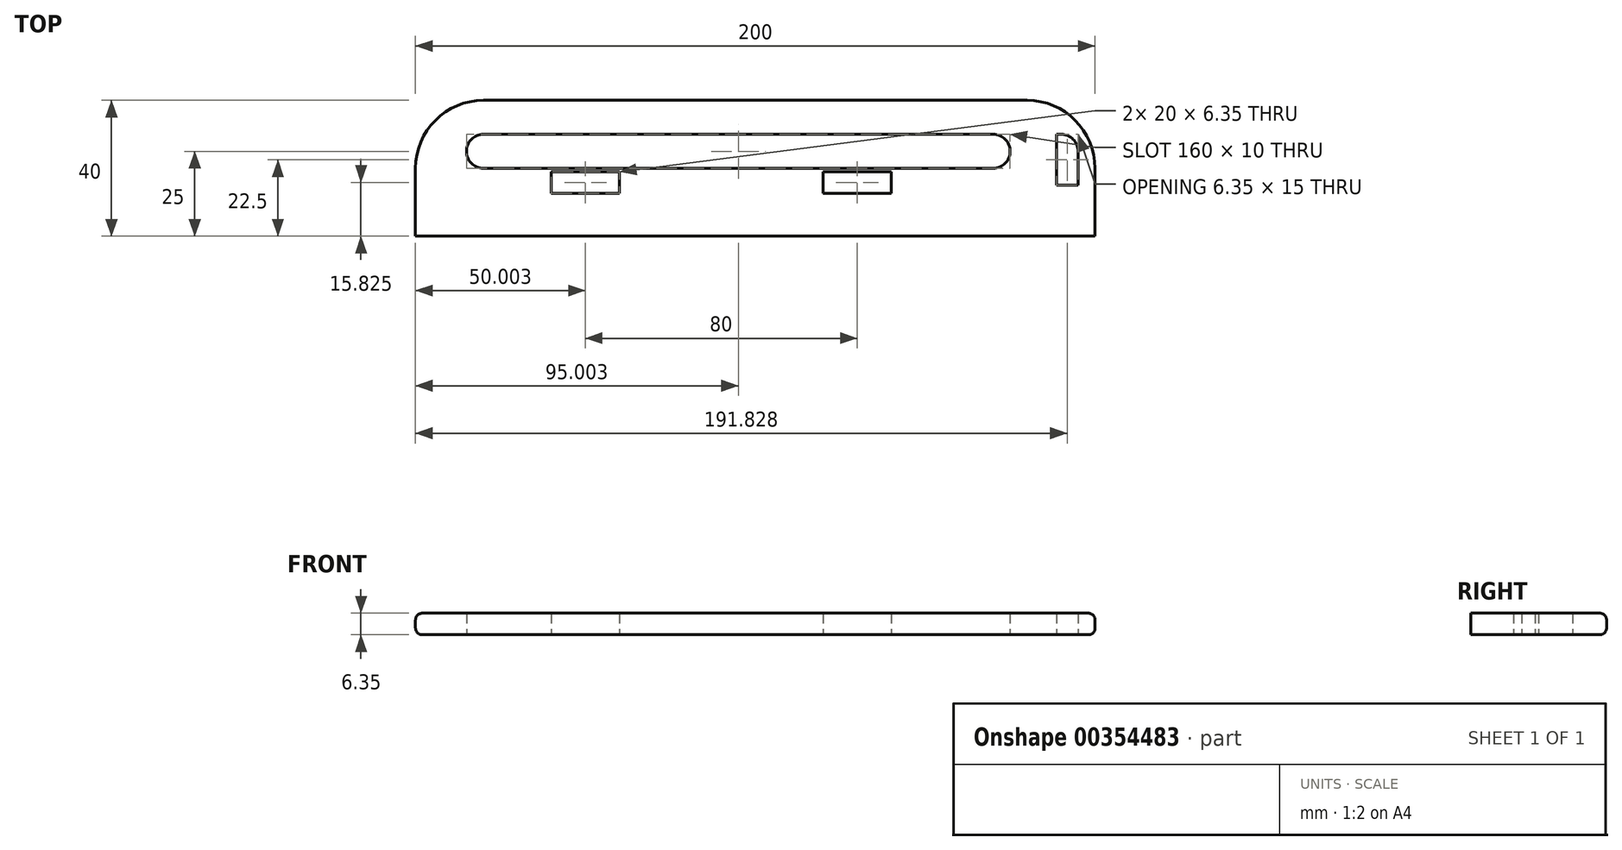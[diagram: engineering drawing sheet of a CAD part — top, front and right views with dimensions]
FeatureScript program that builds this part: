
annotation { "Feature Type Name" : "Feature", "Feature Type Description" : "" }
export const myFeature = defineFeature(function(context is Context, id is Id, definition is map)
    precondition{}
    {
        {
            var Q0;
            Q0=qCreatedBy(makeId("Top.planeOp"),FACE);
            var sketch = newSketch(context, id + "F0", { "sketchPlane" : qUnion([Q0])});
            skLineSegment(sketch, "E0.bottom", {"start": v(-71.36, 10) * mm, "end": v(88.64, 10) * mm});
            skLineSegment(sketch, "E0.top", {"start": v(-91.36, -30) * mm, "end": v(108.64, -30) * mm});
            skLineSegment(sketch, "E0.left", {"start": v(-91.36, -10) * mm, "end": v(-91.36, -30) * mm});
            skLineSegment(sketch, "E0.right", {"start": v(108.64, -10) * mm, "end": v(108.64, -30) * mm});
            skPoint(sketch, "E1.visualSharp", {"position": v(-91.36, 10) * mm});
            skArc(sketch, "E1.filletArc", {"start": v(-71.36, 10) * mm, "mid": v(-85.5, 4.14) * mm, "end": v(-91.36, -10) * mm});
            skPoint(sketch, "E2.visualSharp", {"position": v(108.64, 10) * mm});
            skArc(sketch, "E2.filletArc", {"start": v(108.64, -10) * mm, "mid": v(102.78, 4.14) * mm, "end": v(88.64, 10) * mm});
            skLineSegment(sketch, "E3.bottom", {"start": v(-71.36, 0) * mm, "end": v(78.64, 0) * mm});
            skLineSegment(sketch, "E3.top", {"start": v(-71.36, -10) * mm, "end": v(78.64, -10) * mm});
            skLineSegment(sketch, "E3.left", {"start": v(-71.36, 0) * mm, "end": v(-71.36, -10) * mm});
            skLineSegment(sketch, "E3.right", {"start": v(78.64, 0) * mm, "end": v(78.64, -10) * mm});
            skCircle(sketch, "E4", {"center": v(78.64, -5) * mm, "radius": 5 * mm});
            skCircle(sketch, "E5", {"center": v(-71.36, -5) * mm, "radius": 5 * mm});
            skLineSegment(sketch, "E6.bottom", {"start": v(-51.36, -11) * mm, "end": v(-31.36, -11) * mm});
            skLineSegment(sketch, "E6.top", {"start": v(-51.36, -17.35) * mm, "end": v(-31.36, -17.35) * mm});
            skLineSegment(sketch, "E6.left", {"start": v(-51.36, -11) * mm, "end": v(-51.36, -17.35) * mm});
            skLineSegment(sketch, "E6.right", {"start": v(-31.36, -11) * mm, "end": v(-31.36, -17.35) * mm});
            skLineSegment(sketch, "E7.bottom", {"start": v(28.64, -11) * mm, "end": v(48.64, -11) * mm});
            skLineSegment(sketch, "E7.top", {"start": v(28.64, -17.35) * mm, "end": v(48.64, -17.35) * mm});
            skLineSegment(sketch, "E7.left", {"start": v(28.64, -11) * mm, "end": v(28.64, -17.35) * mm});
            skLineSegment(sketch, "E7.right", {"start": v(48.64, -11) * mm, "end": v(48.64, -17.35) * mm});
            skLineSegment(sketch, "E8.bottom", {"start": v(97.3, 0) * mm, "end": v(98.64, 0) * mm});
            skLineSegment(sketch, "E8.top", {"start": v(97.3, -15) * mm, "end": v(103.64, -15) * mm});
            skLineSegment(sketch, "E8.left", {"start": v(97.3, 0) * mm, "end": v(97.3, -15) * mm});
            skLineSegment(sketch, "E8.right", {"start": v(103.64, -5) * mm, "end": v(103.64, -15) * mm});
            skLineSegment(sketch, "E9.bottom", {"start": v(-61.36, -30) * mm, "end": v(-41.36, -30) * mm});
            skLineSegment(sketch, "E9.top", {"start": v(-61.36, -36.35) * mm, "end": v(-41.36, -36.35) * mm});
            skLineSegment(sketch, "E9.left", {"start": v(-61.36, -30) * mm, "end": v(-61.36, -36.35) * mm});
            skLineSegment(sketch, "E9.right", {"start": v(-41.36, -30) * mm, "end": v(-41.36, -36.35) * mm});
            skLineSegment(sketch, "E10.bottom", {"start": v(58.64, -30) * mm, "end": v(78.64, -30) * mm});
            skLineSegment(sketch, "E10.top", {"start": v(58.64, -36.35) * mm, "end": v(78.64, -36.35) * mm});
            skLineSegment(sketch, "E10.left", {"start": v(58.64, -30) * mm, "end": v(58.64, -36.35) * mm});
            skLineSegment(sketch, "E10.right", {"start": v(78.64, -30) * mm, "end": v(78.64, -36.35) * mm});
            skPoint(sketch, "E11.visualSharp", {"position": v(103.64, 0) * mm});
            skArc(sketch, "E11.filletArc", {"start": v(103.64, -5) * mm, "mid": v(102.18, -1.46) * mm, "end": v(98.64, 0) * mm});
            skSolve(sketch);
        }
        {
            var Q0;
            Q0=makeQuery(id+"F0.imprint","IMPRINT",FACE,{"disambiguationData":[TD([[makeQuery(id+"F0.imprint","IMPRINT",EDGE,{"derivedFrom":sQuery(id+"F0.wireOp",EDGE,"E0.bottom")}),-1.0]])]});
            var Q1;
            Q1=makeQuery(id+"F0.imprint","IMPRINT",FACE,{"disambiguationData":[TD([[makeQuery(id+"F0.imprint","IMPRINT",EDGE,{"derivedFrom":sQuery(id+"F0.wireOp",EDGE,"E9.bottom")}),-1.0]])]});
            var Q2;
            Q2=makeQuery(id+"F0.imprint","IMPRINT",FACE,{"disambiguationData":[TD([[makeQuery(id+"F0.imprint","IMPRINT",EDGE,{"derivedFrom":sQuery(id+"F0.wireOp",EDGE,"E10.bottom")}),-1.0]])]});
            extrude(context, id + "F1", {"entities" : qUnion([Q0, Q1, Q2]), "depth" : 6.35 * mm});
        }
        {
            var Q0;
            Q0=makeQuery(id+"F1.opExtrude","CAP_EDGE",EDGE,{"disambiguationData":[OSD([sQuery(id+"F0.wireOp",EDGE,"E1.filletArc")])],"isStart":false});
            var Q1;
            Q1=makeQuery(id+"F1.opExtrude","CAP_EDGE",EDGE,{"disambiguationData":[OSD([sQuery(id+"F0.wireOp",EDGE,"E0.bottom")])],"isStart":true});
            var Q2;
            Q2=makeQuery(id+"F1.opExtrude","CAP_EDGE",EDGE,{"disambiguationData":[OSD([sQuery(id+"F0.wireOp",EDGE,"E9.top")])],"isStart":true});
            var Q3;
            Q3=makeQuery(id+"F1.opExtrude","CAP_EDGE",EDGE,{"disambiguationData":[OSD([sQuery(id+"F0.wireOp",EDGE,"E10.top")])],"isStart":true});
            fillet(context, id + "F2", {"entities" : qUnion([Q0, Q1, Q2, Q3]), "radius" : 2 * mm, "tangentPropagation" : true, "allowEdgeOverflow" : false});
        }
    });
